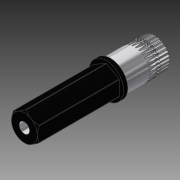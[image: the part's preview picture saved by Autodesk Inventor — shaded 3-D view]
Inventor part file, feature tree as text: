
AUTODESK INVENTOR PART (.ipt)
format: ipt  version: 2014 SP1 (Build 180222100, 222)  size: 2,146,816 bytes
history: native  units: in
note: dims shown in document units (in); Inventor stores cm internally (conversion verified against a paired STEP export)
features: fillet x1, imported_body x1
ambient origin geometry x8: Origin, YZ Plane, XZ Plane, XY Plane, X Axis, Y Axis, Z Axis, Center Point
bodies: Body1 (feature_tree)
feature tree (2):
  fillet  "Fillet5"  [1 undecoded]
  imported_body  "Base1"
note: 1 required parameter value undecoded (feature->parameter linkage not recoverable at this tier; creation-order binding heuristic only, values carry confidence <= 0.55)
